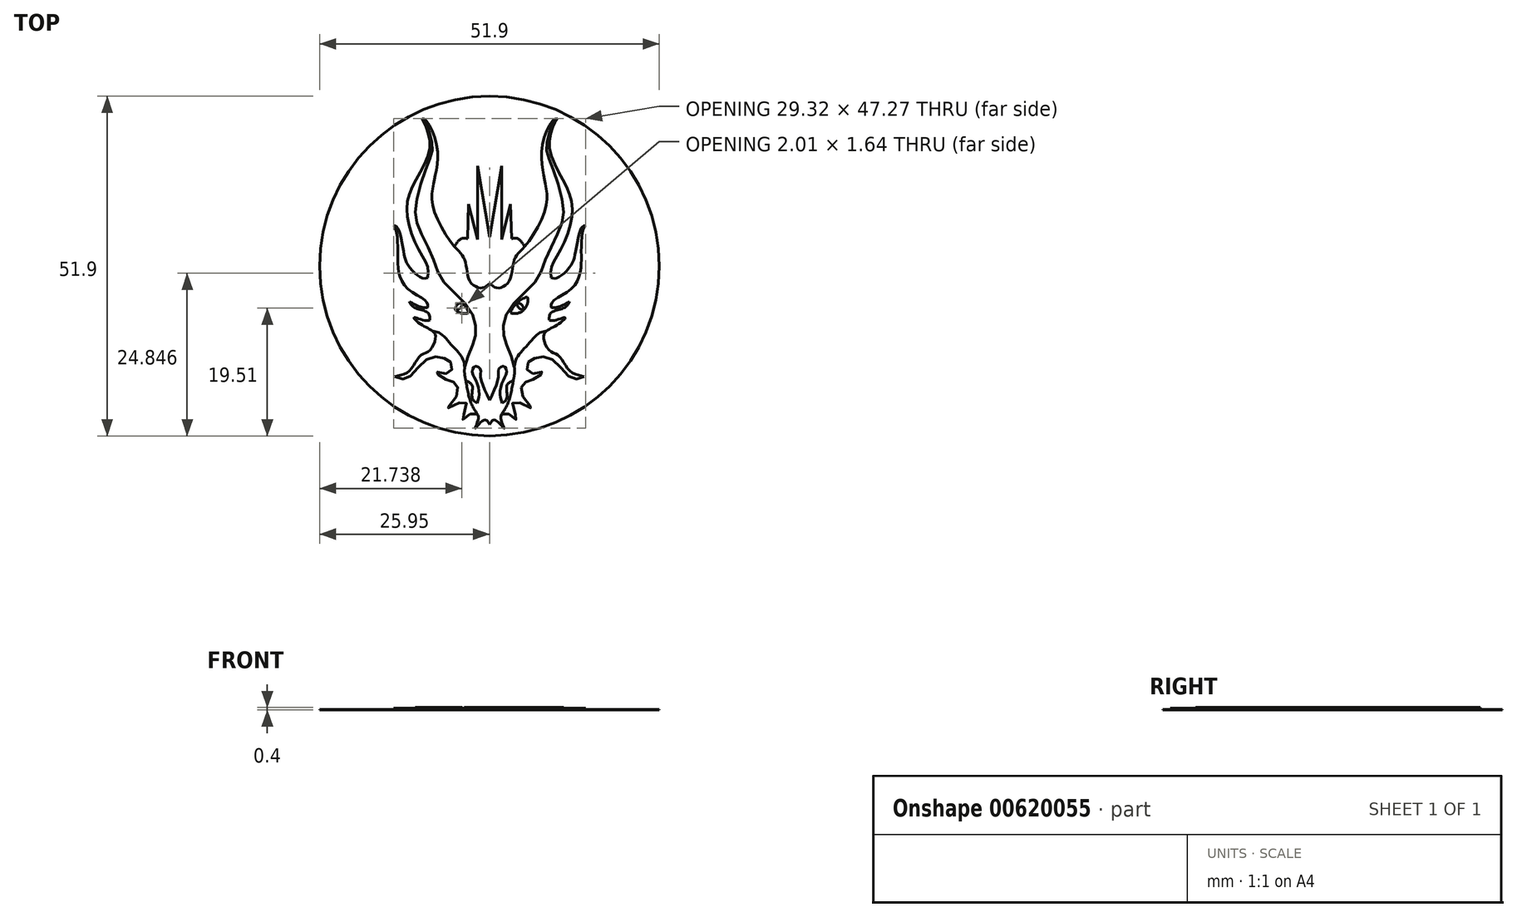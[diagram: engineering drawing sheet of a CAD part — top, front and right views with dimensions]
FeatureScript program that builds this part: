
annotation { "Feature Type Name" : "Feature", "Feature Type Description" : "" }
export const myFeature = defineFeature(function(context is Context, id is Id, definition is map)
    precondition{}
    {
        {
            var Q0;
            Q0=qCreatedBy(makeId("Top.planeOp"),FACE);
            var sketch = newSketch(context, id + "F0", { "sketchPlane" : qUnion([Q0])});
            skCircle(sketch, "E0", {"center": v(0, 0) * mm, "radius": 25.95 * mm});
            skFitSpline(sketch, "E1", {"points": [v(0, -2.64) * mm, v(1.22, -3.33) * mm, v(3, -2.3) * mm, v(3.77, 0.92) * mm, v(5.36, 2.98) * mm, v(8.56, 8.78) * mm, v(8.64, 12.1) * mm, v(8.2, 14.38) * mm, v(8.06, 18.41) * mm, v(9.71, 22.26) * mm, v(10.34, 22.53) * mm], "startDerivative": vector(15.63, -13.98) * mm, "endDerivative": vector(12.07, 1.52) * mm});
            skFitSpline(sketch, "E2", {"points": [v(10.34, 22.53) * mm, v(9.71, 21.32) * mm, v(9.13, 18.19) * mm, v(10.7, 14.11) * mm, v(12.4, 10.49) * mm, v(12.45, 6.77) * mm, v(10.8, 2.4) * mm, v(9.5, 0) * mm, v(9.41, -1.8) * mm], "startDerivative": vector(-7.48, -12.64) * mm, "endDerivative": vector(1.53, -19.09) * mm});
            skFitSpline(sketch, "E3", {"points": [v(9.41, -1.8) * mm, v(10.34, -1.8) * mm, v(12.37, 0) * mm, v(13.11, 2.03) * mm, v(14.05, 5.86) * mm, v(14.66, 6.23) * mm], "startDerivative": vector(6.01, -1.52) * mm, "endDerivative": vector(5.23, 1.12) * mm});
            skFitSpline(sketch, "E4", {"points": [v(14.66, 6.23) * mm, v(14.26, 5.4) * mm, v(14.02, 2.3) * mm, v(13.97, -0.26) * mm, v(12.69, -3.3) * mm, v(9.71, -5.36) * mm, v(9.41, -6.3) * mm], "startDerivative": vector(-4.17, -6.11) * mm, "endDerivative": vector(-0.24, -8.68) * mm});
            skFitSpline(sketch, "E5", {"points": [v(9.41, -6.3) * mm, v(10.34, -6.3) * mm, v(12.23, -5.42) * mm], "startDerivative": vector(2.15, -0.3) * mm, "endDerivative": vector(3.4, 1.92) * mm});
            skFitSpline(sketch, "E6", {"points": [v(12.23, -5.42) * mm, v(11.55, -6.3) * mm, v(9.41, -7.13) * mm, v(9.13, -8.27) * mm], "startDerivative": vector(-1.45, -3.43) * mm, "endDerivative": vector(0.2, -4.34) * mm});
            skFitSpline(sketch, "E7", {"points": [v(9.13, -8.27) * mm, v(10.08, -8.27) * mm, v(11.55, -7.9) * mm, v(10.6, -8.8) * mm, v(8.72, -9.92) * mm, v(8.25, -10.8) * mm, v(9.13, -12.86) * mm, v(10.59, -13.73) * mm, v(12.23, -15.97) * mm, v(14.46, -16.89) * mm], "startDerivative": vector(9.48, -1.74) * mm, "endDerivative": vector(18.58, -3.86) * mm});
            skFitSpline(sketch, "E8", {"points": [v(14.46, -16.89) * mm, v(12.53, -17.14) * mm, v(9.71, -14.32) * mm, v(7.12, -14) * mm, v(5.79, -14.99) * mm, v(6.23, -16.38) * mm, v(8.16, -16.2) * mm, v(6.9, -17.2) * mm, v(5.22, -17.93) * mm, v(5.06, -19.9) * mm, v(6.45, -21.73) * mm, v(3.6, -20.75) * mm, v(4.17, -23.44) * mm, v(2.62, -22.46) * mm, v(1.7, -23.06) * mm, v(2.21, -24.8) * mm, v(0.85, -23.54) * mm, v(0, -24.2) * mm], "startDerivative": vector(-33.47, -14.5) * mm, "endDerivative": vector(-16.04, -27.67) * mm});
            skFitSpline(sketch, "E9", {"points": [v(1.88, -22.6) * mm, v(2.94, -20.61) * mm, v(3.63, -17.5) * mm, v(3.79, -15.46) * mm, v(2.62, -12.11) * mm, v(2.09, -9.6) * mm, v(3.2, -6.35) * mm, v(7.12, -2.22) * mm, v(8.71, 1.36) * mm, v(10.85, 5.98) * mm, v(11.27, 9.14) * mm, v(9.71, 14.84) * mm, v(8.78, 17.43) * mm, v(8.87, 19.26) * mm, v(9.7, 21.77) * mm, v(10.34, 22.53) * mm], "startDerivative": vector(20.89, 31.45) * mm, "endDerivative": vector(17.28, 15.63) * mm});
            skFitSpline(sketch, "E10", {"points": [v(3.63, -17.5) * mm, v(2.62, -18.3) * mm, v(2.62, -20.22) * mm, v(0, -21.73) * mm], "startDerivative": vector(-5.04, -2.15) * mm, "endDerivative": vector(-8.63, -2.8) * mm});
            skFitSpline(sketch, "E11", {"points": [v(1.92, -20.97) * mm, v(1.59, -19.5) * mm, v(2.08, -17.5) * mm, v(2.62, -16.19) * mm, v(2.21, -15.3) * mm, v(1.4, -15.74) * mm, v(1.36, -16.89) * mm, v(0, -20.49) * mm], "startDerivative": vector(-3.53, 9.9) * mm, "endDerivative": vector(-8.82, -18.3) * mm});
            skFitSpline(sketch, "E12", {"points": [v(3.79, -15.46) * mm, v(4.17, -14) * mm, v(5.79, -12.07) * mm, v(7.54, -10.28) * mm, v(8.72, -9.92) * mm], "startDerivative": vector(0.86, 6.52) * mm, "endDerivative": vector(5.84, 0.82) * mm});
            skLineSegment(sketch, "E13", {"start": v(0, 4.47) * mm, "end": v(1.84, 15.3) * mm});
            skLineSegment(sketch, "E14", {"start": v(1.84, 15.3) * mm, "end": v(1.84, 4.09) * mm});
            skLineSegment(sketch, "E15", {"start": v(1.84, 4.09) * mm, "end": v(3.2, 9.47) * mm});
            skLineSegment(sketch, "E16", {"start": v(3.2, 9.47) * mm, "end": v(3.35, 4.19) * mm});
            skFitSpline(sketch, "E17", {"points": [v(3.35, 4.19) * mm, v(4.34, 4.19) * mm, v(5.36, 2.98) * mm], "startDerivative": vector(2.32, 0.48) * mm, "endDerivative": vector(1.73, -2.76) * mm});
            skArc(sketch, "E18", {"start": v(5.78, -4.73) * mm, "mid": v(4.18, -5.62) * mm, "end": v(3.2, -7.17) * mm});
            skArc(sketch, "E19", {"start": v(3.2, -7.17) * mm, "mid": v(5.22, -6.7) * mm, "end": v(5.78, -4.73) * mm});
            skArc(sketch, "E20", {"start": v(5.22, -6.7) * mm, "mid": v(4.94, -5.93) * mm, "end": v(4.18, -5.62) * mm});
            skArc(sketch, "E21", {"start": v(4.18, -5.62) * mm, "mid": v(4.46, -6.39) * mm, "end": v(5.22, -6.7) * mm});
            skArc(sketch, "E22.MirrorCS", {"start": v(-5.22, -6.7) * mm, "mid": v(-4.94, -5.93) * mm, "end": v(-4.18, -5.62) * mm});
            skArc(sketch, "E23.MirrorCS", {"start": v(-5.78, -4.73) * mm, "mid": v(-4.18, -5.62) * mm, "end": v(-3.2, -7.17) * mm});
            skArc(sketch, "E24.MirrorCS", {"start": v(-4.18, -5.62) * mm, "mid": v(-4.46, -6.39) * mm, "end": v(-5.22, -6.7) * mm});
            skArc(sketch, "E25.MirrorCS", {"start": v(-3.2, -7.17) * mm, "mid": v(-5.22, -6.7) * mm, "end": v(-5.78, -4.73) * mm});
            skFitSpline(sketch, "E26.MirrorCS", {"points": [v(-1.92, -20.97) * mm, v(-1.59, -19.5) * mm, v(-2.08, -17.5) * mm, v(-2.62, -16.19) * mm, v(-2.21, -15.3) * mm, v(-1.4, -15.74) * mm, v(-1.36, -16.89) * mm, v(0, -20.49) * mm], "startDerivative": vector(3.53, 9.9) * mm, "endDerivative": vector(8.82, -18.3) * mm});
            skFitSpline(sketch, "E27.MirrorCS", {"points": [v(-3.63, -17.5) * mm, v(-2.62, -18.3) * mm, v(-2.62, -20.22) * mm, v(0, -21.73) * mm], "startDerivative": vector(5.04, -2.15) * mm, "endDerivative": vector(8.63, -2.8) * mm});
            skFitSpline(sketch, "E28.MirrorCS", {"points": [v(-14.46, -16.89) * mm, v(-12.53, -17.14) * mm, v(-9.71, -14.32) * mm, v(-7.12, -14) * mm, v(-5.79, -14.99) * mm, v(-6.23, -16.38) * mm, v(-8.16, -16.2) * mm, v(-6.9, -17.2) * mm, v(-5.22, -17.93) * mm, v(-5.06, -19.9) * mm, v(-6.45, -21.73) * mm, v(-3.6, -20.75) * mm, v(-4.17, -23.44) * mm, v(-2.62, -22.46) * mm, v(-1.7, -23.06) * mm, v(-2.21, -24.8) * mm, v(-0.85, -23.54) * mm, v(0, -24.2) * mm], "startDerivative": vector(33.47, -14.5) * mm, "endDerivative": vector(16.04, -27.67) * mm});
            skFitSpline(sketch, "E29.MirrorCS", {"points": [v(-3.79, -15.46) * mm, v(-4.17, -14) * mm, v(-5.79, -12.07) * mm, v(-7.54, -10.28) * mm, v(-8.72, -9.92) * mm], "startDerivative": vector(-0.86, 6.52) * mm, "endDerivative": vector(-5.84, 0.82) * mm});
            skFitSpline(sketch, "E30.MirrorCS", {"points": [v(-9.41, -6.3) * mm, v(-10.34, -6.3) * mm, v(-12.23, -5.42) * mm], "startDerivative": vector(-2.15, -0.3) * mm, "endDerivative": vector(-3.4, 1.92) * mm});
            skFitSpline(sketch, "E31.MirrorCS", {"points": [v(-12.23, -5.42) * mm, v(-11.55, -6.3) * mm, v(-9.41, -7.13) * mm, v(-9.13, -8.27) * mm], "startDerivative": vector(1.45, -3.43) * mm, "endDerivative": vector(-0.2, -4.34) * mm});
            skFitSpline(sketch, "E32.MirrorCS", {"points": [v(-9.13, -8.27) * mm, v(-10.08, -8.27) * mm, v(-11.55, -7.9) * mm, v(-10.6, -8.8) * mm, v(-8.72, -9.92) * mm, v(-8.25, -10.8) * mm, v(-9.13, -12.86) * mm, v(-10.59, -13.73) * mm, v(-12.23, -15.97) * mm, v(-14.46, -16.89) * mm], "startDerivative": vector(-9.48, -1.74) * mm, "endDerivative": vector(-18.58, -3.86) * mm});
            skFitSpline(sketch, "E33.MirrorCS", {"points": [v(-9.41, -1.8) * mm, v(-10.34, -1.8) * mm, v(-12.37, 0) * mm, v(-13.11, 2.03) * mm, v(-14.05, 5.86) * mm, v(-14.66, 6.23) * mm], "startDerivative": vector(-6.01, -1.52) * mm, "endDerivative": vector(-5.23, 1.12) * mm});
            skFitSpline(sketch, "E34.MirrorCS", {"points": [v(-14.66, 6.23) * mm, v(-14.26, 5.4) * mm, v(-14.02, 2.3) * mm, v(-13.97, -0.26) * mm, v(-12.69, -3.3) * mm, v(-9.71, -5.36) * mm, v(-9.41, -6.3) * mm], "startDerivative": vector(4.17, -6.11) * mm, "endDerivative": vector(0.24, -8.68) * mm});
            skFitSpline(sketch, "E35.MirrorCS", {"points": [v(-10.34, 22.53) * mm, v(-9.71, 21.32) * mm, v(-9.13, 18.19) * mm, v(-10.7, 14.11) * mm, v(-12.4, 10.49) * mm, v(-12.45, 6.77) * mm, v(-10.8, 2.4) * mm, v(-9.5, 0) * mm, v(-9.41, -1.8) * mm], "startDerivative": vector(7.48, -12.64) * mm, "endDerivative": vector(-1.53, -19.09) * mm});
            skFitSpline(sketch, "E36.MirrorCS", {"points": [v(-1.88, -22.6) * mm, v(-2.94, -20.61) * mm, v(-3.63, -17.5) * mm, v(-3.79, -15.46) * mm, v(-2.62, -12.11) * mm, v(-2.09, -9.6) * mm, v(-3.2, -6.35) * mm, v(-7.12, -2.22) * mm, v(-8.71, 1.36) * mm, v(-10.85, 5.98) * mm, v(-11.27, 9.14) * mm, v(-9.71, 14.84) * mm, v(-8.78, 17.43) * mm, v(-8.87, 19.26) * mm, v(-9.7, 21.77) * mm, v(-10.34, 22.53) * mm], "startDerivative": vector(-20.89, 31.45) * mm, "endDerivative": vector(-17.28, 15.63) * mm});
            skFitSpline(sketch, "E37.MirrorCS", {"points": [v(0, -2.64) * mm, v(-1.22, -3.33) * mm, v(-3, -2.3) * mm, v(-3.77, 0.92) * mm, v(-5.36, 2.98) * mm, v(-8.56, 8.78) * mm, v(-8.64, 12.1) * mm, v(-8.2, 14.38) * mm, v(-8.06, 18.41) * mm, v(-9.71, 22.26) * mm, v(-10.34, 22.53) * mm], "startDerivative": vector(-15.63, -13.98) * mm, "endDerivative": vector(-12.07, 1.52) * mm});
            skFitSpline(sketch, "E38.MirrorCS", {"points": [v(-3.35, 4.19) * mm, v(-4.34, 4.19) * mm, v(-5.36, 2.98) * mm], "startDerivative": vector(-2.32, 0.48) * mm, "endDerivative": vector(-1.73, -2.76) * mm});
            skLineSegment(sketch, "E39.MirrorCS", {"start": v(-3.2, 9.47) * mm, "end": v(-3.35, 4.19) * mm});
            skLineSegment(sketch, "E40.MirrorCS", {"start": v(-1.84, 4.09) * mm, "end": v(-3.2, 9.47) * mm});
            skLineSegment(sketch, "E41.MirrorCS", {"start": v(-1.84, 15.3) * mm, "end": v(-1.84, 4.09) * mm});
            skLineSegment(sketch, "E42.MirrorCS", {"start": v(0, 4.47) * mm, "end": v(-1.84, 15.3) * mm});
            skSolve(sketch);
        }
        {
            var Q0;
            {var subQ11=sQuery(id+"F0.wireOp",EDGE,"E2");Q0=makeQuery(id+"F0.imprint","IMPRINT",FACE,{"disambiguationData":[TD([[makeQuery(id+"F0.imprint","IMPRINT",EDGE,{"derivedFrom":subQ11}),-1.0]])]});}
            var Q1;
            {var subQ1=sQuery(id+"F0.wireOp",EDGE,"E29.MirrorCS");Q1=makeQuery(id+"F0.imprint","IMPRINT",FACE,{"disambiguationData":[TD([[makeQuery(id+"F0.imprint","IMPRINT",EDGE,{"derivedFrom":subQ1}),-1.0]])]});}
            var Q2;
            Q2=makeQuery(id+"F0.imprint","IMPRINT",FACE,{"disambiguationData":[TD([[makeQuery(id+"F0.imprint","IMPRINT",EDGE,{"derivedFrom":sQuery(id+"F0.wireOp",EDGE,"E22.MirrorCS")}),-1.0]])]});
            var Q3;
            Q3=makeQuery(id+"F0.imprint","IMPRINT",FACE,{"disambiguationData":[TD([[makeQuery(id+"F0.imprint","IMPRINT",EDGE,{"derivedFrom":sQuery(id+"F0.wireOp",EDGE,"E20")}),1.0]])]});
            var Q4;
            {var subQ3=sQuery(id+"F0.wireOp",EDGE,"E11");Q4=makeQuery(id+"F0.imprint","IMPRINT",FACE,{"disambiguationData":[TD([[makeQuery(id+"F0.imprint","IMPRINT",EDGE,{"derivedFrom":subQ3}),1.0]])]});}
            var Q5;
            {var subQ8=sQuery(id+"F0.wireOp",EDGE,"E8");var subQ11=sQuery(id+"F0.wireOp",EDGE,"E28.MirrorCS");var subQ13=makeQuery(id+"F0.imprint","INTERSECT",VERTEX,{"derivedFrom":[subQ8,subQ11]});Q5=makeQuery(id+"F0.imprint","IMPRINT",FACE,{"disambiguationData":[TD([[makeQuery(id+"F0.imprint","IMPRINT",EDGE,{"disambiguationData":[TD([[subQ13,1.0]])],"derivedFrom":subQ8}),-1.0]])]});}
            extrude(context, id + "F1", {"entities" : qUnion([Q0, Q1, Q2, Q3, Q4, Q5]), "depth" : .3 * mm, "offsetDistance" : 25.4 * mm});
        }
        {
            var Q0;
            {var subQ3=sQuery(id+"F0.wireOp",EDGE,"E29.MirrorCS");Q0=makeQuery(id+"F0.imprint","IMPRINT",FACE,{"disambiguationData":[TD([[makeQuery(id+"F0.imprint","IMPRINT",EDGE,{"derivedFrom":subQ3}),1.0]])]});}
            var Q1;
            {var subQ2=sQuery(id+"F0.wireOp",EDGE,"E12");Q1=makeQuery(id+"F0.imprint","IMPRINT",FACE,{"disambiguationData":[TD([[makeQuery(id+"F0.imprint","IMPRINT",EDGE,{"derivedFrom":subQ2}),-1.0]])]});}
            var Q2;
            Q2=makeQuery(id+"F0.imprint","IMPRINT",FACE,{"disambiguationData":[TD([[makeQuery(id+"F0.imprint","IMPRINT",EDGE,{"derivedFrom":sQuery(id+"F0.wireOp",EDGE,"E13")}),-1.0]])]});
            extrude(context, id + "F2", {"entities" : qUnion([Q0, Q1, Q2]), "depth" : .3 * mm, "offsetDistance" : 25.4 * mm});
        }
        {
            var Q0;
            {var subQ6=sQuery(id+"F0.wireOp",EDGE,"E11");Q0=makeQuery(id+"F0.imprint","IMPRINT",FACE,{"disambiguationData":[TD([[makeQuery(id+"F0.imprint","IMPRINT",EDGE,{"derivedFrom":subQ6}),-1.0]])]});}
            extrude(context, id + "F3", {"entities" : qUnion([Q0]), "depth" : .4 * mm, "offsetDistance" : 25.4 * mm});
        }
        {
            var Q0;
            Q0=makeQuery(id+"F0.imprint","IMPRINT",FACE,{"disambiguationData":[TD([[makeQuery(id+"F0.imprint","IMPRINT",EDGE,{"derivedFrom":sQuery(id+"F0.wireOp",EDGE,"E0")}),1.0]])]});
            extrude(context, id + "F4", {"entities" : qUnion([Q0]), "depth" : .1 * mm, "offsetDistance" : 25.4 * mm});
        }
        {
            var Q0;
            {var subQ0=sQuery(id+"F0.wireOp",EDGE,"E24.MirrorCS");Q0=makeQuery(id+"F0.imprint","IMPRINT",FACE,{"disambiguationData":[TD([[makeQuery(id+"F0.imprint","IMPRINT",EDGE,{"derivedFrom":subQ0}),1.0]])]});}
            var Q1;
            {var subQ0=sQuery(id+"F0.wireOp",EDGE,"E22.MirrorCS");Q1=makeQuery(id+"F0.imprint","IMPRINT",FACE,{"disambiguationData":[TD([[makeQuery(id+"F0.imprint","IMPRINT",EDGE,{"derivedFrom":subQ0}),1.0]])]});}
            var Q2;
            {var subQ3=sQuery(id+"F0.wireOp",EDGE,"E21");Q2=makeQuery(id+"F0.imprint","IMPRINT",FACE,{"disambiguationData":[TD([[makeQuery(id+"F0.imprint","IMPRINT",EDGE,{"derivedFrom":subQ3}),-1.0]])]});}
            var Q3;
            {var subQ4=sQuery(id+"F0.wireOp",EDGE,"E20");Q3=makeQuery(id+"F0.imprint","IMPRINT",FACE,{"disambiguationData":[TD([[makeQuery(id+"F0.imprint","IMPRINT",EDGE,{"derivedFrom":subQ4}),-1.0]])]});}
            extrude(context, id + "F5", {"entities" : qUnion([Q0, Q1, Q2, Q3]), "operationType" : NewBodyOperationType.ADD, "depth" : 0.4 * mm, "offsetDistance" : 25.4 * mm, "hasDraft" : true, "draftAngle" : 1 * degree});
        }
    });
